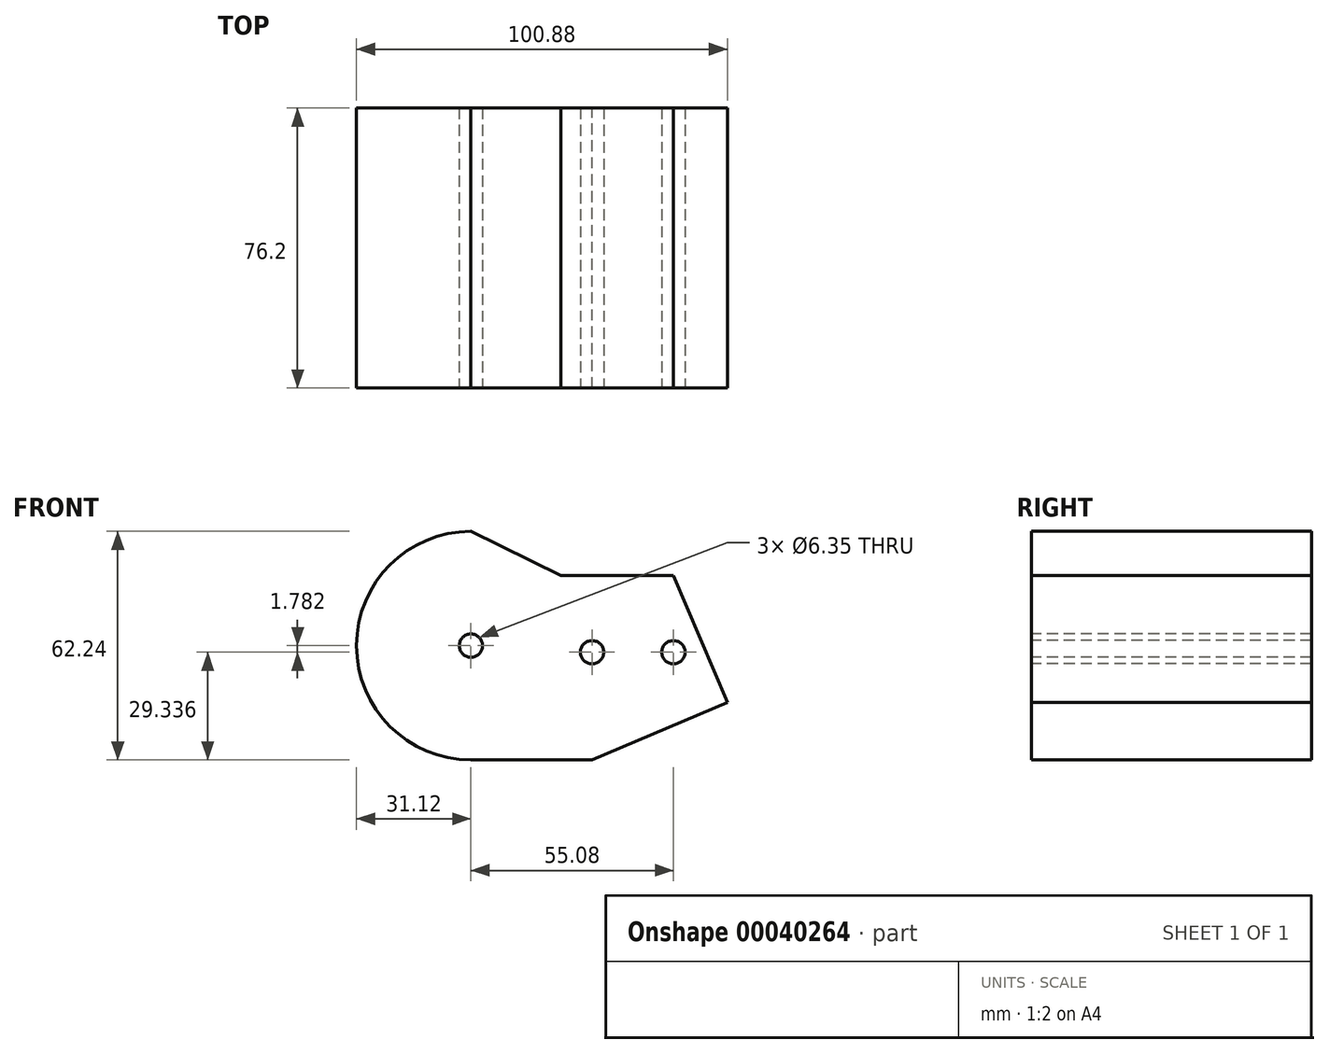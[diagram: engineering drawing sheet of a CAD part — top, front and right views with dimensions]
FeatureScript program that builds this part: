
annotation { "Feature Type Name" : "Feature", "Feature Type Description" : "" }
export const myFeature = defineFeature(function(context is Context, id is Id, definition is map)
    precondition{}
    {
        {
            var Q0;
            Q0=qCreatedBy(makeId("Front.planeOp"),FACE);
            var sketch = newSketch(context, id + "F0", { "sketchPlane" : qUnion([Q0])});
            skLineSegment(sketch, "E0", {"start": v(0, 62.24) * mm, "end": v(24.42, 50.2) * mm});
            skLineSegment(sketch, "E1", {"start": v(24.42, 50.2) * mm, "end": v(55.08, 50.2) * mm});
            skLineSegment(sketch, "E2", {"start": v(55.08, 50.2) * mm, "end": v(69.76, 15.64) * mm});
            skLineSegment(sketch, "E3", {"start": v(69.76, 15.64) * mm, "end": v(32.94, 0) * mm});
            skLineSegment(sketch, "E4", {"start": v(32.94, 0) * mm, "end": v(0, 0) * mm});
            skArc(sketch, "E5", {"start": v(0, 0) * mm, "mid": v(-31.12, 31.12) * mm, "end": v(0, 62.24) * mm});
            skSolve(sketch);
        }
        {
            var Q0;
            Q0=makeQuery(id+"F0.imprint","IMPRINT",FACE,{"disambiguationData":[TD([[makeQuery(id+"F0.imprint","IMPRINT",EDGE,{"derivedFrom":sQuery(id+"F0.wireOp",EDGE,"E0")}),-1.0]])]});
            extrude(context, id + "F1", {"entities" : qUnion([Q0]), "depth" : 76.2 * mm});
        }
        {
            var Q0;
            Q0=makeQuery(id+"F1.opExtrude","CAP_FACE",FACE,{"disambiguationData":[OSD([sQuery(id+"F0.wireOp",EDGE,"E0"),sQuery(id+"F0.wireOp",EDGE,"E1"),sQuery(id+"F0.wireOp",EDGE,"E2"),sQuery(id+"F0.wireOp",EDGE,"E3"),sQuery(id+"F0.wireOp",EDGE,"E4"),sQuery(id+"F0.wireOp",EDGE,"E5")])],"isStart":false});
            var sketch = newSketch(context, id + "F2", { "sketchPlane" : qUnion([Q0])});
            skPoint(sketch, "E6", {"position": v(0, 31.12) * mm});
            skPoint(sketch, "E7", {"position": v(32.94, 29.34) * mm});
            skPoint(sketch, "E8", {"position": v(12.92, 29.34) * mm});
            skPoint(sketch, "E9", {"position": v(55.08, 29.34) * mm});
            skSolve(sketch);
        }
        {
            var Q0;
            Q0=sQuery(id+"F2.wireOp",VERTEX,"E7");
            var Q1;
            Q1=sQuery(id+"F2.wireOp",VERTEX,"E9");
            var Q2;
            Q2=sQuery(id+"F2.wireOp",VERTEX,"E6");
            var Q3;
            Q3=makeQuery(id+"F1.opExtrude","SWEPT_BODY",BODY,{"disambiguationData":[OSD([sQuery(id+"F0.wireOp",EDGE,"E0"),sQuery(id+"F0.wireOp",EDGE,"E1"),sQuery(id+"F0.wireOp",EDGE,"E2"),sQuery(id+"F0.wireOp",EDGE,"E3"),sQuery(id+"F0.wireOp",EDGE,"E4"),sQuery(id+"F0.wireOp",EDGE,"E5")])]});
            hole(context, id + "F3", {"style" : HoleStyle.SIMPLE, "holeDiameter" : 6.35 * mm, "endStyle" : HoleEndStyle.THROUGH, "locations" : qUnion([Q0, Q1, Q2]), "scope" : qUnion([Q3])});
        }
    });
